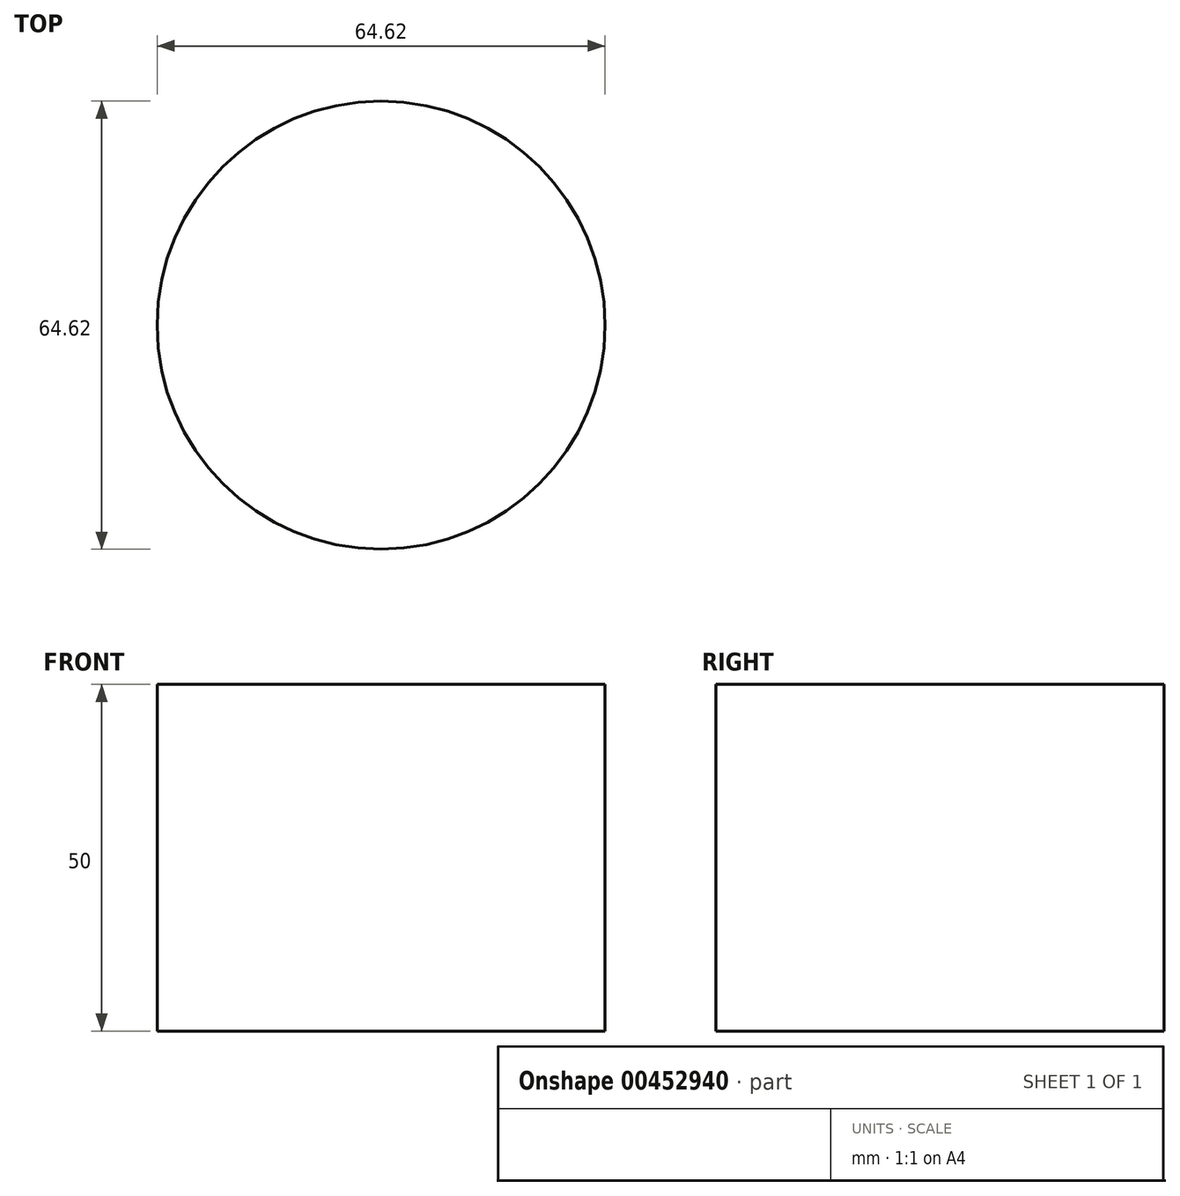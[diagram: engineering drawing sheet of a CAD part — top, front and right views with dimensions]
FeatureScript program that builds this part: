
annotation { "Feature Type Name" : "Feature", "Feature Type Description" : "" }
export const myFeature = defineFeature(function(context is Context, id is Id, definition is map)
    precondition{}
    {
        {
            var Q0;
            Q0=qCreatedBy(makeId("Top.planeOp"),FACE);
            var sketch = newSketch(context, id + "F0", { "sketchPlane" : qUnion([Q0])});
            skCircle(sketch, "E0", {"center": v(0, 0) * mm, "radius": 32.31 * mm});
            skSolve(sketch);
        }
        {
            var Q0;
            Q0 = qSketchRegion(id + "F0", true);
            extrude(context, id + "F1", {"entities" : qUnion([Q0]), "depth" : 50 * mm});
        }
    });
